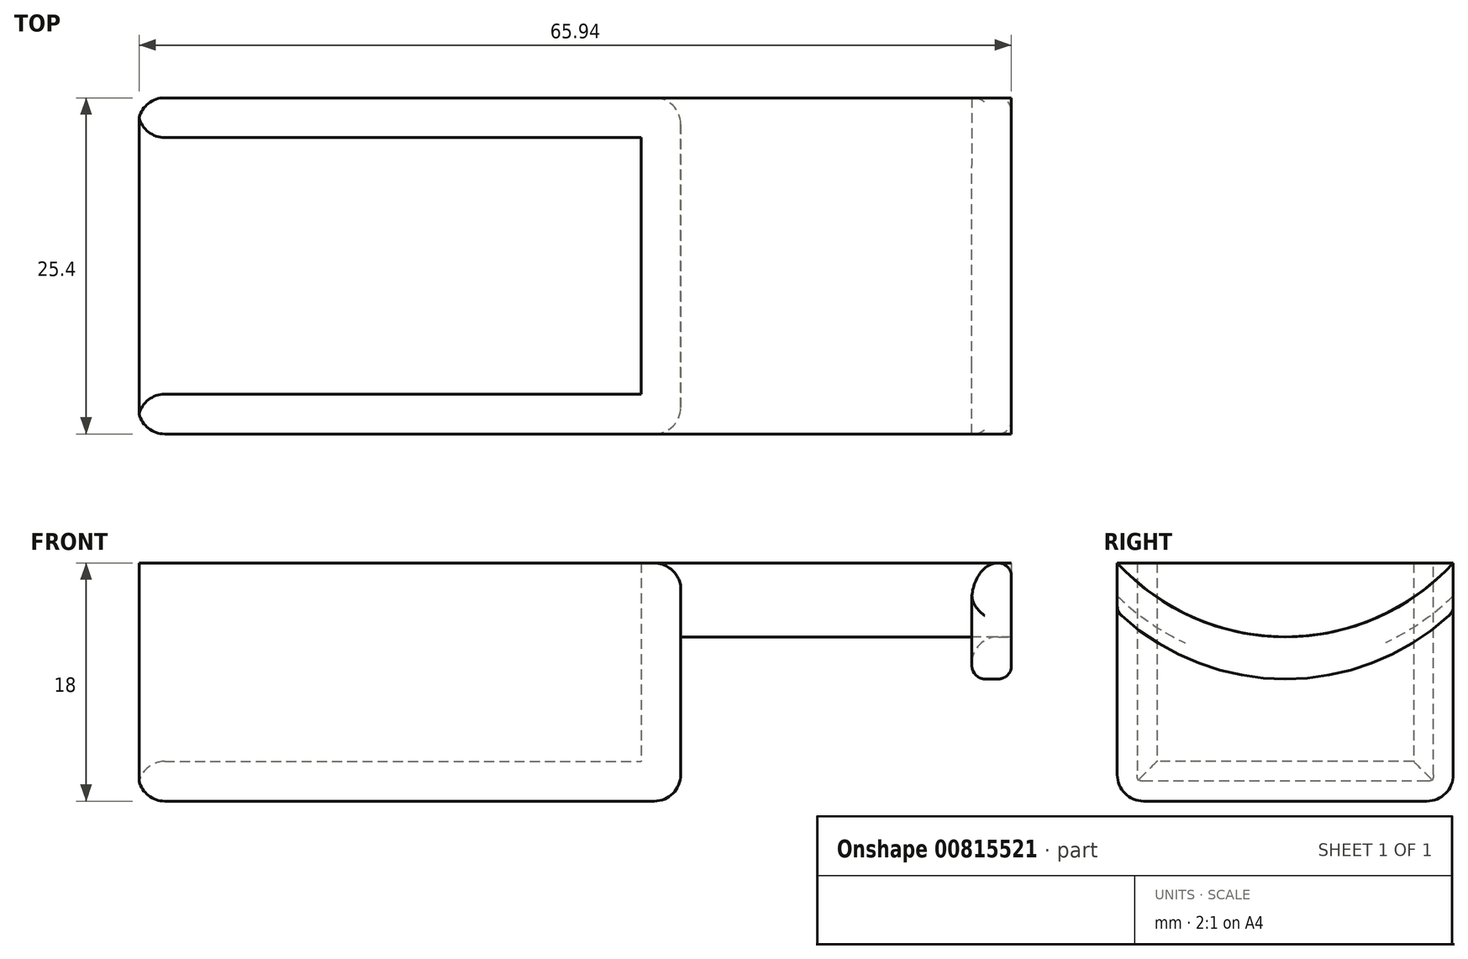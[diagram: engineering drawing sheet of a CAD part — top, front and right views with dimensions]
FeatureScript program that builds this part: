
annotation { "Feature Type Name" : "Feature", "Feature Type Description" : "" }
export const myFeature = defineFeature(function(context is Context, id is Id, definition is map)
    precondition{}
    {
        {
            var Q0;
            Q0=qCreatedBy(makeId("Top.planeOp"),FACE);
            var sketch = newSketch(context, id + "F0", { "sketchPlane" : qUnion([Q0])});
            skLineSegment(sketch, "E0.bottom", {"start": v(0, 0) * mm, "end": v(38, 0) * mm});
            skLineSegment(sketch, "E0.top", {"start": v(0, -25.4) * mm, "end": v(38, -25.4) * mm});
            skLineSegment(sketch, "E0.left", {"start": v(0, 0) * mm, "end": v(0, -25.4) * mm});
            skLineSegment(sketch, "E0.right", {"start": v(38, 0) * mm, "end": v(38, -25.4) * mm});
            skLineSegment(sketch, "E1.top", {"start": v(0, -3) * mm, "end": v(38, -3) * mm});
            skLineSegment(sketch, "E1.left", {"start": v(0, 0) * mm, "end": v(0, -3) * mm});
            skLineSegment(sketch, "E1.right", {"start": v(38, 0) * mm, "end": v(38, -3) * mm});
            skLineSegment(sketch, "E2.top", {"start": v(0, -22.4) * mm, "end": v(38, -22.4) * mm});
            skLineSegment(sketch, "E2.left", {"start": v(0, -25.4) * mm, "end": v(0, -22.4) * mm});
            skLineSegment(sketch, "E2.right", {"start": v(38, -25.4) * mm, "end": v(38, -22.4) * mm});
            skSolve(sketch);
        }
        {
            var Q0;
            {var subQ0=sQuery(id+"F0.wireOp",EDGE,"E0.bottom");Q0=makeQuery(id+"F0.imprint","IMPRINT",FACE,{"disambiguationData":[TD([[makeQuery(id+"F0.imprint","IMPRINT",EDGE,{"derivedFrom":subQ0}),-1.0]])]});}
            var Q1;
            {var subQ0=sQuery(id+"F0.wireOp",EDGE,"E0.top");Q1=makeQuery(id+"F0.imprint","IMPRINT",FACE,{"disambiguationData":[TD([[makeQuery(id+"F0.imprint","IMPRINT",EDGE,{"derivedFrom":subQ0}),1.0]])]});}
            extrude(context, id + "F1", {"entities" : qUnion([Q0, Q1]), "depth" : 15 * mm, "offsetDistance" : 25 * mm});
        }
        {
            var Q0;
            {var subQ0=sQuery(id+"F0.wireOp",EDGE,"E1.top");var subQ8=makeQuery(id+"F0.imprint","IMPRINT",EDGE,{"derivedFrom":subQ0});var subQ10=sQuery(id+"F0.wireOp",EDGE,"E0.top");var subQ11=sQuery(id+"F0.wireOp",EDGE,"E0.bottom");Q0=qUnion([makeQuery(id+"F0.imprint","IMPRINT",FACE,{"disambiguationData":[TD([[makeQuery(id+"F0.imprint","IMPRINT",EDGE,{"derivedFrom":subQ11}),-1.0]])]}),makeQuery(id+"F0.imprint","IMPRINT",FACE,{"disambiguationData":[TD([[makeQuery(id+"F0.imprint","IMPRINT",EDGE,{"derivedFrom":subQ10}),1.0]])]}),makeQuery(id+"F0.imprint","IMPRINT",FACE,{"disambiguationData":[TD([[subQ8,-1.0]])]})]);}
            var Q1;
            Q1=makeQuery(id+"F1.opExtrude","CAP_FACE",FACE,{"disambiguationData":[OSD([sQuery(id+"F0.wireOp",EDGE,"E0.bottom"),sQuery(id+"F0.wireOp",EDGE,"E0.left"),sQuery(id+"F0.wireOp",EDGE,"E0.right"),sQuery(id+"F0.wireOp",EDGE,"E1.top")])],"isStart":true});
            var Q2;
            Q2=makeQuery(id+"F1.opExtrude","CAP_FACE",FACE,{"disambiguationData":[OSD([sQuery(id+"F0.wireOp",EDGE,"E0.top"),sQuery(id+"F0.wireOp",EDGE,"E0.left"),sQuery(id+"F0.wireOp",EDGE,"E0.right"),sQuery(id+"F0.wireOp",EDGE,"E2.top")])],"isStart":true});
            extrude(context, id + "F2", {"entities" : qUnion([Q0, Q1, Q2]), "operationType" : NewBodyOperationType.ADD, "oppositeDirection" : true, "depth" : 3 * mm, "offsetDistance" : 25 * mm});
        }
        {
            var Q0;
            {var subQ0=sQuery(id+"F0.wireOp",EDGE,"E0.right");var subQ1=makeQuery(id+"F0.imprint","INTERSECT",VERTEX,{"derivedFrom":[subQ0,sQuery(id+"F0.wireOp",EDGE,"E1.top")]});var subQ2=makeQuery(id+"F0.imprint","IMPRINT",EDGE,{"disambiguationData":[TD([[makeQuery(id+"F0.imprint","INTERSECT",VERTEX,{"derivedFrom":[sQuery(id+"F0.wireOp",EDGE,"E0.bottom"),subQ0]}),-1.0]])],"derivedFrom":subQ0});var subQ4=makeQuery(id+"F0.imprint","IMPRINT",EDGE,{"disambiguationData":[TD([[makeQuery(id+"F0.imprint","INTERSECT",VERTEX,{"derivedFrom":[sQuery(id+"F0.wireOp",EDGE,"E0.top"),subQ0]}),1.0]])],"derivedFrom":subQ0});Q0=makeQuery(id+"F2.boolean.opBoolean","MERGE",FACE,{"derivedFrom":[makeQuery(id+"F1.opExtrude","SWEPT_FACE",FACE,{"disambiguationData":[OSD([subQ0]),TDD([subQ4])]}),makeQuery(id+"F1.opExtrude","SWEPT_FACE",FACE,{"disambiguationData":[OSD([subQ0]),TDD([subQ2])]}),makeQuery(id+"F2.opExtrude","SWEPT_FACE",FACE,{"disambiguationData":[OSD([subQ0]),TDD([makeQuery(id+"F0.imprint","IMPRINT",EDGE,{"disambiguationData":[TD([[subQ1,-1.0]])],"derivedFrom":subQ0}),subQ4,subQ2])]})]});}
            var sketch = newSketch(context, id + "F3", { "sketchPlane" : qUnion([Q0])});
            skLineSegment(sketch, "E3.bottom", {"start": v(0, 15) * mm, "end": v(-25.4, 15) * mm});
            skLineSegment(sketch, "E3.top", {"start": v(0, -3) * mm, "end": v(-25.4, -3) * mm});
            skLineSegment(sketch, "E3.left", {"start": v(0, 15) * mm, "end": v(0, -3) * mm});
            skLineSegment(sketch, "E3.right", {"start": v(-25.4, 15) * mm, "end": v(-25.4, -3) * mm});
            skSolve(sketch);
        }
        {
            var Q0;
            Q0=makeQuery(id+"F3.imprint","IMPRINT",FACE,{"disambiguationData":[TD([[makeQuery(id+"F3.imprint","IMPRINT",EDGE,{"derivedFrom":sQuery(id+"F3.wireOp",EDGE,"E3.top")}),-1.0]])]});
            var Q1;
            {var subQ1=sQuery(id+"F0.wireOp",EDGE,"E1.top");var subQ2=sQuery(id+"F0.wireOp",EDGE,"E0.right");var subQ3=makeQuery(id+"F1.opExtrude","SWEPT_EDGE",EDGE,{"disambiguationData":[OSD([subQ2,subQ1])]});Q1=makeQuery(id+"F3.imprint","IMPRINT",FACE,{"disambiguationData":[TD([[makeQuery(id+"F3.imprint","IMPRINT",EDGE,{"derivedFrom":subQ3}),-1.0]])]});}
            extrude(context, id + "F4", {"entities" : qUnion([Q0, Q1]), "operationType" : NewBodyOperationType.ADD, "depth" : 3 * mm, "offsetDistance" : 25 * mm});
        }
        {
            var Q0;
            Q0=makeQuery(id+"F4.opExtrude","CAP_FACE",FACE,{"disambiguationData":[OSD([sQuery(id+"F3.wireOp",EDGE,"E3.bottom"),sQuery(id+"F3.wireOp",EDGE,"E3.top"),sQuery(id+"F3.wireOp",EDGE,"E3.left"),sQuery(id+"F3.wireOp",EDGE,"E3.right")])],"isStart":false});
            var sketch = newSketch(context, id + "F5", { "sketchPlane" : qUnion([Q0])});
            skArc(sketch, "E4", {"start": v(-25.4, 15) * mm, "mid": v(-12.7, 9.4) * mm, "end": v(0, 15) * mm});
            skLineSegment(sketch, "E5", {"start": v(0, 15) * mm, "end": v(-25.4, 15) * mm});
            skSolve(sketch);
        }
        {
            var Q0;
            Q0=makeQuery(id+"F5.imprint","IMPRINT",FACE,{"disambiguationData":[TD([[makeQuery(id+"F5.imprint","IMPRINT",EDGE,{"derivedFrom":sQuery(id+"F5.wireOp",EDGE,"E4")}),1.0]])]});
            extrude(context, id + "F6", {"entities" : qUnion([Q0]), "operationType" : NewBodyOperationType.ADD, "depth" : 25 * mm, "offsetDistance" : 25 * mm});
        }
        {
            var Q0;
            Q0=makeQuery(id+"F6.opExtrude","CAP_FACE",FACE,{"disambiguationData":[OSD([sQuery(id+"F5.wireOp",EDGE,"E4"),sQuery(id+"F5.wireOp",EDGE,"E5")])],"isStart":false});
            var sketch = newSketch(context, id + "F7", { "sketchPlane" : qUnion([Q0])});
            skLineSegment(sketch, "E6.bottom", {"start": v(0, 15) * mm, "end": v(-25.4, 15) * mm});
            skLineSegment(sketch, "E6.left", {"start": v(0, 15) * mm, "end": v(0, 11.31) * mm});
            skLineSegment(sketch, "E6.right", {"start": v(-25.4, 15) * mm, "end": v(-25.4, 11.31) * mm});
            skArc(sketch, "E7", {"start": v(-25.4, 11.31) * mm, "mid": v(-12.7, 6.23) * mm, "end": v(0, 11.31) * mm});
            skPoint(sketch, "E8.orphan", {"position": v(0, 7.63) * mm});
            skPoint(sketch, "E9.orphan", {"position": v(-25.4, 7.63) * mm});
            skSolve(sketch);
        }
        {
            var Q0;
            Q0=makeQuery(id+"F7.imprint","IMPRINT",FACE,{"disambiguationData":[TD([[makeQuery(id+"F7.imprint","IMPRINT",EDGE,{"derivedFrom":sQuery(id+"F7.wireOp",EDGE,"E6.left")}),-1.0]])]});
            extrude(context, id + "F8", {"entities" : qUnion([Q0]), "oppositeDirection" : true, "depth" : 3 * mm, "offsetDistance" : 25 * mm});
        }
        {
            var Q0;
            {var subQ0=sQuery(id+"F0.wireOp",EDGE,"E0.bottom");Q0=makeQuery(id+"F4.boolean.opBoolean","MERGE",EDGE,{"derivedFrom":[makeQuery(id+"F2.opExtrude","CAP_EDGE",EDGE,{"disambiguationData":[OSD([subQ0]),TDD([makeQuery(id+"F0.imprint","IMPRINT",EDGE,{"derivedFrom":subQ0})])],"isStart":false}),makeQuery(id+"F4.opExtrude","SWEPT_EDGE",EDGE,{"disambiguationData":[OSD([sQuery(id+"F3.wireOp",EDGE,"E3.top"),sQuery(id+"F3.wireOp",EDGE,"E3.left")])]})]});}
            var Q1;
            Q1=makeQuery(id+"F4.opExtrude","CAP_EDGE",EDGE,{"disambiguationData":[OSD([sQuery(id+"F3.wireOp",EDGE,"E3.left")])],"isStart":false});
            var Q2;
            Q2=makeQuery(id+"F4.opExtrude","CAP_EDGE",EDGE,{"disambiguationData":[OSD([sQuery(id+"F3.wireOp",EDGE,"E3.top")])],"isStart":false});
            var Q3;
            {var subQ0=sQuery(id+"F0.wireOp",EDGE,"E0.top");Q3=makeQuery(id+"F4.boolean.opBoolean","MERGE",EDGE,{"derivedFrom":[makeQuery(id+"F2.opExtrude","CAP_EDGE",EDGE,{"disambiguationData":[OSD([subQ0]),TDD([makeQuery(id+"F0.imprint","IMPRINT",EDGE,{"derivedFrom":subQ0})])],"isStart":false}),makeQuery(id+"F4.opExtrude","SWEPT_EDGE",EDGE,{"disambiguationData":[OSD([sQuery(id+"F3.wireOp",EDGE,"E3.top"),sQuery(id+"F3.wireOp",EDGE,"E3.right")])]})]});}
            var Q4;
            {var subQ0=sQuery(id+"F0.wireOp",EDGE,"E0.left");var subQ1=sQuery(id+"F0.wireOp",EDGE,"E0.bottom");Q4=makeQuery(id+"F2.boolean.opBoolean","MERGE",EDGE,{"derivedFrom":[makeQuery(id+"F1.opExtrude","SWEPT_EDGE",EDGE,{"disambiguationData":[OSD([subQ1,subQ0])]}),makeQuery(id+"F2.opExtrude","SWEPT_EDGE",EDGE,{"disambiguationData":[OSD([subQ1,subQ0]),TDD([makeQuery(id+"F0.imprint","INTERSECT",VERTEX,{"derivedFrom":[subQ1,subQ0]})])]})]});}
            var Q5;
            {var subQ0=sQuery(id+"F0.wireOp",EDGE,"E0.left");var subQ1=makeQuery(id+"F0.imprint","INTERSECT",VERTEX,{"derivedFrom":[subQ0,sQuery(id+"F0.wireOp",EDGE,"E1.top")]});Q5=makeQuery(id+"F2.opExtrude","CAP_EDGE",EDGE,{"disambiguationData":[OSD([subQ0]),TDD([makeQuery(id+"F0.imprint","IMPRINT",EDGE,{"disambiguationData":[TD([[subQ1,-1.0]])],"derivedFrom":subQ0}),makeQuery(id+"F0.imprint","IMPRINT",EDGE,{"disambiguationData":[TD([[makeQuery(id+"F0.imprint","INTERSECT",VERTEX,{"derivedFrom":[sQuery(id+"F0.wireOp",EDGE,"E0.top"),subQ0]}),1.0]])],"derivedFrom":subQ0}),makeQuery(id+"F0.imprint","IMPRINT",EDGE,{"disambiguationData":[TD([[makeQuery(id+"F0.imprint","INTERSECT",VERTEX,{"derivedFrom":[sQuery(id+"F0.wireOp",EDGE,"E0.bottom"),subQ0]}),-1.0]])],"derivedFrom":subQ0})])],"isStart":false});}
            var Q6;
            Q6=makeQuery(id+"F4.opExtrude","CAP_EDGE",EDGE,{"disambiguationData":[OSD([sQuery(id+"F3.wireOp",EDGE,"E3.right")])],"isStart":false});
            var Q7;
            {var subQ0=sQuery(id+"F0.wireOp",EDGE,"E0.left");var subQ1=sQuery(id+"F0.wireOp",EDGE,"E0.top");Q7=makeQuery(id+"F2.boolean.opBoolean","MERGE",EDGE,{"derivedFrom":[makeQuery(id+"F1.opExtrude","SWEPT_EDGE",EDGE,{"disambiguationData":[OSD([subQ1,subQ0])]}),makeQuery(id+"F2.opExtrude","SWEPT_EDGE",EDGE,{"disambiguationData":[OSD([subQ1,subQ0]),TDD([makeQuery(id+"F0.imprint","INTERSECT",VERTEX,{"derivedFrom":[subQ1,subQ0]})])]})]});}
            var Q8;
            {var subQ0=sQuery(id+"F0.wireOp",EDGE,"E0.left");var subQ1=makeQuery(id+"F0.imprint","INTERSECT",VERTEX,{"derivedFrom":[subQ0,sQuery(id+"F0.wireOp",EDGE,"E1.top")]});Q8=makeQuery(id+"F2.opExtrude","CAP_EDGE",EDGE,{"disambiguationData":[OSD([subQ0]),TDD([makeQuery(id+"F0.imprint","IMPRINT",EDGE,{"disambiguationData":[TD([[subQ1,-1.0]])],"derivedFrom":subQ0}),makeQuery(id+"F0.imprint","IMPRINT",EDGE,{"disambiguationData":[TD([[makeQuery(id+"F0.imprint","INTERSECT",VERTEX,{"derivedFrom":[sQuery(id+"F0.wireOp",EDGE,"E0.top"),subQ0]}),1.0]])],"derivedFrom":subQ0}),makeQuery(id+"F0.imprint","IMPRINT",EDGE,{"disambiguationData":[TD([[makeQuery(id+"F0.imprint","INTERSECT",VERTEX,{"derivedFrom":[sQuery(id+"F0.wireOp",EDGE,"E0.bottom"),subQ0]}),-1.0]])],"derivedFrom":subQ0})])],"isStart":true});}
            var Q9;
            Q9=makeQuery(id+"F1.opExtrude","SWEPT_EDGE",EDGE,{"disambiguationData":[OSD([sQuery(id+"F0.wireOp",EDGE,"E0.left"),sQuery(id+"F0.wireOp",EDGE,"E2.top")])]});
            var Q10;
            Q10=makeQuery(id+"F1.opExtrude","SWEPT_EDGE",EDGE,{"disambiguationData":[OSD([sQuery(id+"F0.wireOp",EDGE,"E0.left"),sQuery(id+"F0.wireOp",EDGE,"E1.top")])]});
            fillet(context, id + "F9", {"entities" : qUnion([Q0, Q1, Q2, Q3, Q4, Q5, Q6, Q7, Q8, Q9, Q10]), "radius" : 2 * mm, "tangentPropagation" : true, "allowEdgeOverflow" : false});
        }
        {
            var Q0;
            Q0=makeQuery(id+"F8.opExtrude","SWEPT_FACE",FACE,{"disambiguationData":[OSD([sQuery(id+"F7.wireOp",EDGE,"E7")])]});
            var Q1;
            Q1=makeQuery(id+"F8.opExtrude","CAP_EDGE",EDGE,{"disambiguationData":[OSD([sQuery(id+"F7.wireOp",EDGE,"E6.right")])],"isStart":true});
            var Q2;
            Q2=makeQuery(id+"F8.opExtrude","CAP_EDGE",EDGE,{"disambiguationData":[OSD([sQuery(id+"F7.wireOp",EDGE,"E6.left")])],"isStart":true});
            fillet(context, id + "F10", {"entities" : qUnion([Q0, Q1, Q2]), "radius" : 1 * mm, "tangentPropagation" : true, "allowEdgeOverflow" : false});
        }
        {
            var Q0;
            Q0=makeQuery(id+"F6.opExtrude","CAP_EDGE",EDGE,{"disambiguationData":[OSD([sQuery(id+"F5.wireOp",EDGE,"E4")])],"isStart":true});
            var Q1;
            Q1=makeQuery(id+"F8.opExtrude","CAP_EDGE",EDGE,{"disambiguationData":[OSD([sQuery(id+"F5.wireOp",EDGE,"E4")])],"isStart":false});
            fillet(context, id + "F11", {"entities" : qUnion([Q0, Q1]), "radius" : 2 * mm, "tangentPropagation" : true, "allowEdgeOverflow" : false});
        }
    });
